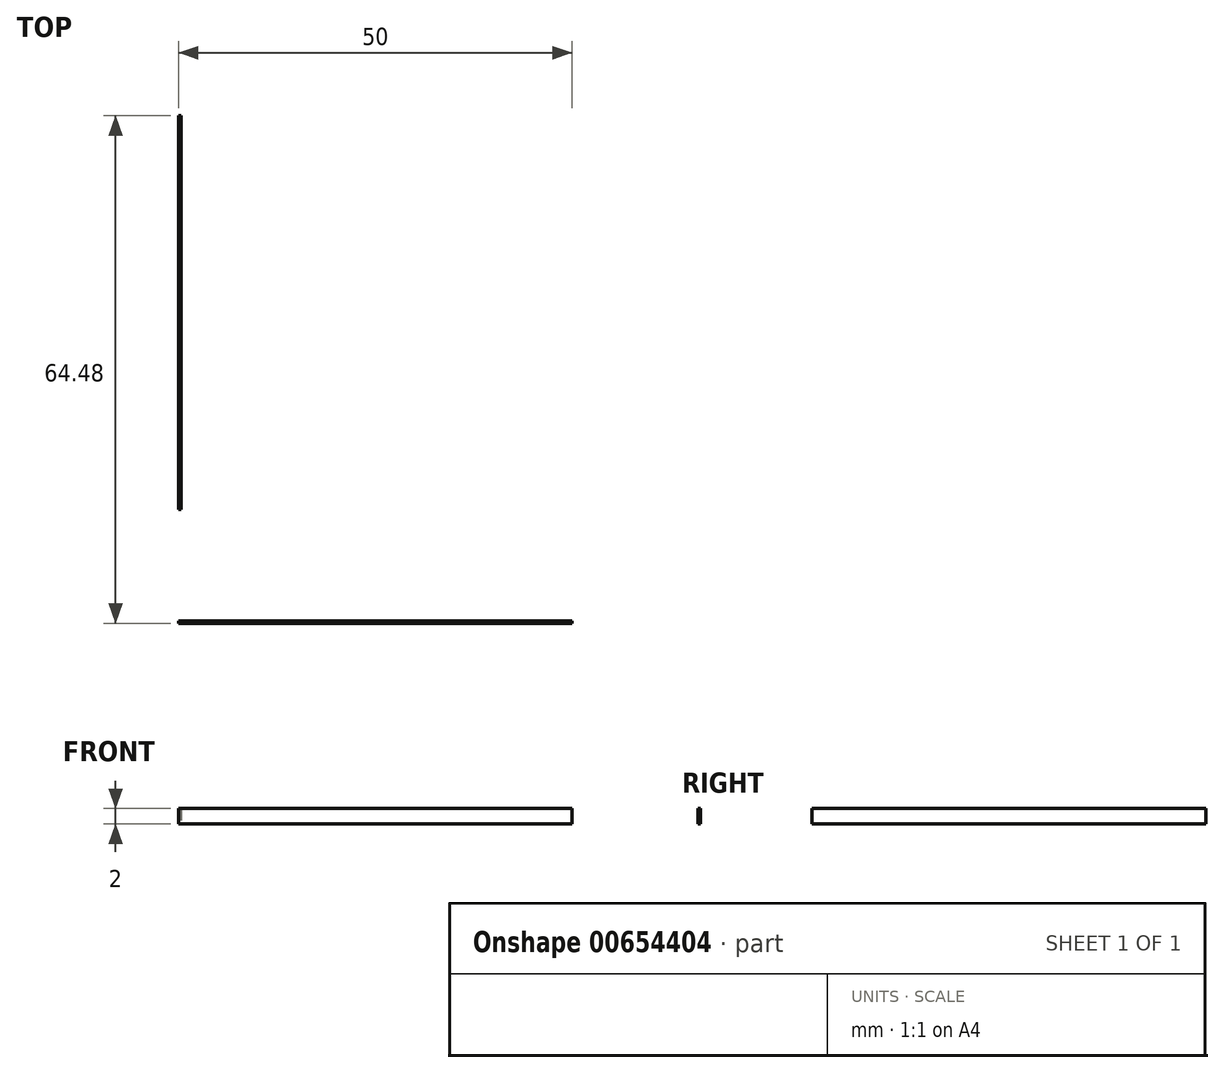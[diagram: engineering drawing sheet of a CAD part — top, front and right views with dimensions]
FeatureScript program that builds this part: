
annotation { "Feature Type Name" : "Feature", "Feature Type Description" : "" }
export const myFeature = defineFeature(function(context is Context, id is Id, definition is map)
    precondition{}
    {
        {
            var Q0;
            Q0=qCreatedBy(makeId("Top.planeOp"),FACE);
            var sketch = newSketch(context, id + "F0", { "sketchPlane" : qUnion([Q0])});
            skLineSegment(sketch, "E0.bottom", {"start": v(-36.8, -48.72) * mm, "end": v(13.2, -48.72) * mm});
            skLineSegment(sketch, "E0.top", {"start": v(-36.8, -49.02) * mm, "end": v(13.2, -49.02) * mm});
            skLineSegment(sketch, "E0.left", {"start": v(-36.8, -48.72) * mm, "end": v(-36.8, -49.02) * mm});
            skLineSegment(sketch, "E0.right", {"start": v(13.2, -48.72) * mm, "end": v(13.2, -49.02) * mm});
            skLineSegment(sketch, "E1.bottom", {"start": v(-36.8, -34.54) * mm, "end": v(-36.5, -34.54) * mm});
            skLineSegment(sketch, "E1.top", {"start": v(-36.8, 15.46) * mm, "end": v(-36.5, 15.46) * mm});
            skLineSegment(sketch, "E1.left", {"start": v(-36.8, -34.54) * mm, "end": v(-36.8, 15.46) * mm});
            skLineSegment(sketch, "E1.right", {"start": v(-36.5, -34.54) * mm, "end": v(-36.5, 15.46) * mm});
            skSolve(sketch);
        }
        {
            var Q0;
            Q0 = qSketchRegion(id + "F0", true);
            extrude(context, id + "F1", {"entities" : qUnion([Q0]), "depth" : 2 * mm, "offsetDistance" : 25 * mm});
        }
    });
